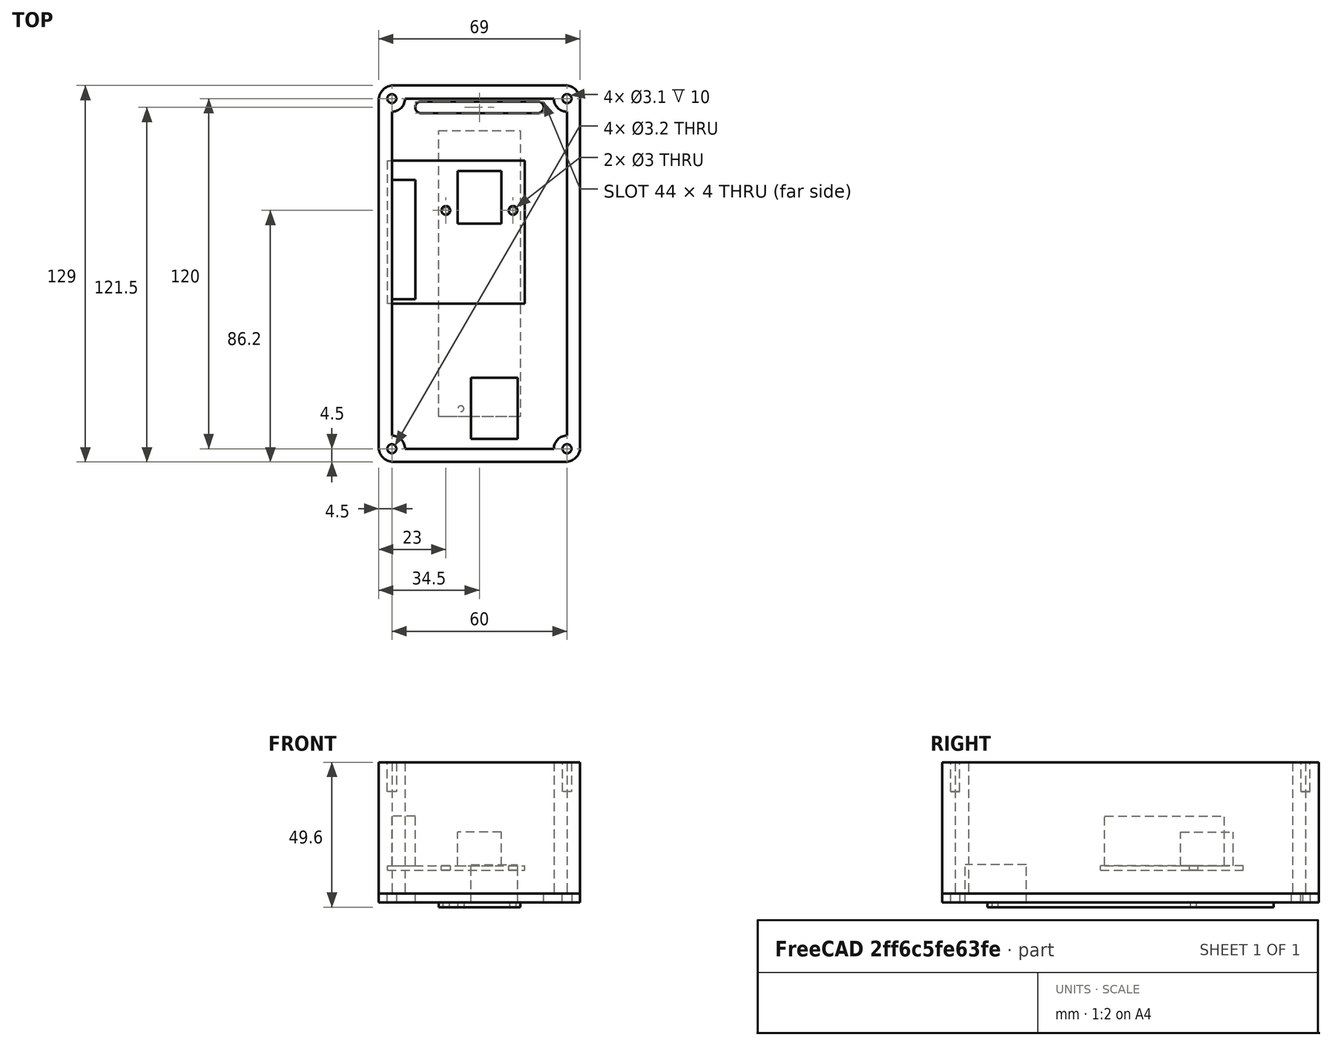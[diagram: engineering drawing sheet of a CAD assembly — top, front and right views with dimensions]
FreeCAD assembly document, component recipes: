
FREECAD ASSEMBLY — COMPONENT RECIPES ("Olimex_ESP32_POE_ISO_iot_case")

This assembly document has 3 components, labeled P0..P2 below (a component is one placed body or linked part). 3 of them carry a construction recipe — the FreeCAD feature program that regenerates the part from scratch, quoted from this document or its linked companion documents; the rest are supplied as boundary geometry only. No exploded tour is included for this assembly.
COMPONENT P0 — recipe-attached ("Box", modeled in this document).
Construction recipe (the document's own serialized feature program — sketch geometry with constraints, then the solid features built on it; lengths are millimeters unless a unit is written):

FEATURE [PartDesign::CoordinateSystem] LCS_0002
  AttacherType = Attacher::AttachEngine3D
  MapMode = 2
  Support = -> [X_Axis003]
FEATURE [PartDesign::Plane] DatumPlane002  label="Box Body Outer Bottom"
  Length = 87.869
  MapMode = 5
  ResizeMode = 0
  Support = -> [XY_Plane003]
  Width = 147.869
FEATURE [PartDesign::Plane] DatumPlane003  label="Box Body Inner Bottom"
  AttachmentOffset = pos=(0,0,3) rot=(0,0,1;0rad)
  Length = 87.869
  MapMode = 5
  Placement = pos=(0,0,3) rot=(0,0,1;0rad)
  ResizeMode = 0
  Support = -> [XY_Plane003]
  Width = 147.869
  expr: .AttachmentOffset.Base.z = Variables.base_thickness
FEATURE [PartDesign::Plane] DatumPlane004  label="Box Body Top"
  AttachmentOffset = pos=(0,0,45) rot=(0,0,1;0rad)
  Length = 87.869
  MapMode = 5
  Placement = pos=(0,0,48) rot=(0,0,1;0rad)
  ResizeMode = 0
  Support = -> [DatumPlane003]
  Width = 147.869
  expr: .AttachmentOffset.Base.z = Variables.inner_depth
FEATURE [Sketcher::SketchObject] Sketch002
  FullyConstrained = true
  MapMode = 5
  Support = -> [DatumPlane002]
  expr: .Constraints.height = Variables.inner_height + 2 * Variables.wall_thickness
  expr: .Constraints.width = Variables.inner_width + 2 * Variables.wall_thickness
  expr: Constraints[29] = Variables.corner_radius
  sketch-geometry (12):
    g0: LineSegment StartX=-34.5 StartY=64.5 StartZ=0 EndX=34.5 EndY=64.5 EndZ=0
    g1: LineSegment StartX=34.5 StartY=64.5 StartZ=0 EndX=34.5 EndY=-64.5 EndZ=0
    g2: LineSegment StartX=34.5 StartY=-64.5 StartZ=0 EndX=-34.5 EndY=-64.5 EndZ=0
    g3: LineSegment StartX=-34.5 StartY=-64.5 StartZ=0 EndX=-34.5 EndY=64.5 EndZ=0
    g4: LineSegment StartX=-29.5 StartY=64.5 StartZ=0 EndX=29.5 EndY=64.5 EndZ=0
    g5: LineSegment StartX=34.5 StartY=59.5 StartZ=0 EndX=34.5 EndY=-59.5 EndZ=0
    g6: LineSegment StartX=29.5 StartY=-64.5 StartZ=0 EndX=-29.5 EndY=-64.5 EndZ=0
    g7: LineSegment StartX=-34.5 StartY=-59.5 StartZ=0 EndX=-34.5 EndY=59.5 EndZ=0
    g8: ArcOfCircle CenterX=-29.5 CenterY=59.5 CenterZ=0 NormalX=0 NormalY=0 NormalZ=1 AngleXU=0 Radius=5 StartAngle=1.5708 EndAngle=3.14159
    g9: ArcOfCircle CenterX=-29.5 CenterY=-59.5 CenterZ=0 NormalX=0 NormalY=0 NormalZ=1 AngleXU=0 Radius=5 StartAngle=3.14159 EndAngle=4.71239
    g10: ArcOfCircle CenterX=29.5 CenterY=-59.5 CenterZ=0 NormalX=0 NormalY=0 NormalZ=1 AngleXU=0 Radius=5 StartAngle=4.71239 EndAngle=6.28319
    g11: ArcOfCircle CenterX=29.5 CenterY=59.5 CenterZ=0 NormalX=0 NormalY=0 NormalZ=1 AngleXU=0 Radius=5 StartAngle=0 EndAngle=1.5708
  constraints (30):
    c: Coincident(g0,g1)
    c: Coincident(g1,g2)
    c: Coincident(g2,g3)
    c: Coincident(g3,g0)
    c: Horizontal(g2)
    c: Vertical(g3)
    c: Symmetric(g0,g0,g-2)
    c: Symmetric(g0,g1,g-1)
    c: DistanceX(g0,g0) = 69  'width'
    c: DistanceY(g1,g1) = 129  'height'
    c: Horizontal(g4)
    c: Horizontal(g6)
    c: Vertical(g5)
    c: Vertical(g7)
    c: Tangent(g4,g8) = 1.5708
    c: Tangent(g7,g8) = 1.5708
    c: Tangent(g7,g9) = 1.5708
    c: Tangent(g6,g9) = 1.5708
    c: Tangent(g6,g10) = 1.5708
    c: Tangent(g5,g10) = 1.5708
    c: Tangent(g4,g11) = 1.5708
    c: Tangent(g5,g11) = 1.5708
    c: Equal(g8,g9)
    c: Equal(g9,g10)
    c: Equal(g10,g11)
    c: PointOnObject(g4,g0)
    c: PointOnObject(g7,g3)
    c: PointOnObject(g5,g1)
    c: PointOnObject(g6,g2)
    c: Radius(g9) = 5
FEATURE [PartDesign::Pad] Pad001  label="Box Body Volume"
  Direction = (0,0,1)
  Length = 10
  Length2 = 10
  Profile = -> Sketch002
  ReferenceAxis = -> Sketch002 [N_Axis]
  Type = 3
  UpToFace = -> DatumPlane004 [Plane]
FEATURE [Sketcher::SketchObject] Sketch003
  FullyConstrained = true
  MapMode = 5
  Placement = pos=(0,0,48) rot=(0,0,1;0rad)
  Support = -> [DatumPlane004]
  expr: .Constraints.height = Variables.inner_height
  expr: .Constraints.width = Variables.inner_width
  sketch-geometry (8):
    g0: LineSegment StartX=-30 StartY=60 StartZ=0 EndX=30 EndY=60 EndZ=0
    g1: LineSegment StartX=30 StartY=60 StartZ=0 EndX=30 EndY=-60 EndZ=0
    g2: LineSegment StartX=30 StartY=-60 StartZ=0 EndX=-30 EndY=-60 EndZ=0
    g3: LineSegment StartX=-30 StartY=-60 StartZ=0 EndX=-30 EndY=60 EndZ=0
    g4: LineSegment StartX=-30 StartY=60 StartZ=0 EndX=30 EndY=60 EndZ=0
    g5: LineSegment StartX=30 StartY=60 StartZ=0 EndX=30 EndY=-60 EndZ=0
    g6: LineSegment StartX=30 StartY=-60 StartZ=0 EndX=-30 EndY=-60 EndZ=0
    g7: LineSegment StartX=-30 StartY=-60 StartZ=0 EndX=-30 EndY=60 EndZ=0
  constraints (20):
    c: Coincident(g0,g1)
    c: Coincident(g1,g2)
    c: Coincident(g2,g3)
    c: Coincident(g3,g0)
    c: Horizontal(g2)
    c: Vertical(g3)
    c: Symmetric(g0,g0,g-2)
    c: Symmetric(g0,g1,g-1)
    c: DistanceX(g0,g0) = 60  'width'
    c: DistanceY(g1,g1) = 120  'height'
    c: Coincident(g4,g5)
    c: Coincident(g5,g6)
    c: Coincident(g6,g7)
    c: Coincident(g7,g4)
    c: Horizontal(g4)
    c: Horizontal(g6)
    c: Vertical(g5)
    c: Vertical(g7)
    c: Coincident(g4,g0)
    c: Coincident(g5,g1)
FEATURE [PartDesign::Pocket] Pocket001  label="Box Inner Volume"
  BaseFeature = -> Pad001
  Direction = (0,0,-1)
  Length = 0
  Length2 = 5
  Profile = -> Sketch003
  ReferenceAxis = -> Sketch003 [N_Axis]
  Type = 3
  UpToFace = -> DatumPlane003
FEATURE [Sketcher::SketchObject] Sketch004
  FullyConstrained = true
  MapMode = 5
  Placement = pos=(0,0,48) rot=(0,0,1;0rad)
  Support = -> [DatumPlane004]
  expr: .Constraints.height = Variables.inner_height
  expr: .Constraints.width = Variables.inner_width
  expr: Constraints[41] = Variables.wall_thickness
  sketch-geometry (16):
    g0: LineSegment StartX=-30 StartY=60 StartZ=0 EndX=30 EndY=60 EndZ=0
    g1: LineSegment StartX=30 StartY=60 StartZ=0 EndX=30 EndY=-60 EndZ=0
    g2: LineSegment StartX=30 StartY=-60 StartZ=0 EndX=-30 EndY=-60 EndZ=0
    g3: LineSegment StartX=-30 StartY=-60 StartZ=0 EndX=-30 EndY=60 EndZ=0
    g4: ArcOfCircle CenterX=-30 CenterY=60 CenterZ=0 NormalX=0 NormalY=0 NormalZ=1 AngleXU=0 Radius=4.5 StartAngle=4.71239 EndAngle=6.28319
    g5: LineSegment StartX=-30 StartY=60 StartZ=0 EndX=-30 EndY=55.5 EndZ=0
    g6: LineSegment StartX=-30 StartY=60 StartZ=0 EndX=-25.5 EndY=60 EndZ=0
    g7: ArcOfCircle CenterX=30 CenterY=60 CenterZ=0 NormalX=0 NormalY=0 NormalZ=1 AngleXU=0 Radius=4.5 StartAngle=3.14159 EndAngle=4.71239
    g8: ArcOfCircle CenterX=30 CenterY=-60 CenterZ=0 NormalX=0 NormalY=0 NormalZ=1 AngleXU=0 Radius=4.5 StartAngle=1.5708 EndAngle=3.14159
    g9: ArcOfCircle CenterX=-30 CenterY=-60 CenterZ=0 NormalX=0 NormalY=0 NormalZ=1 AngleXU=0 Radius=4.5 StartAngle=7e-16 EndAngle=1.5708
    g10: LineSegment StartX=-30 StartY=-55.5 StartZ=0 EndX=-30 EndY=-60 EndZ=0
    g11: LineSegment StartX=-30 StartY=-60 StartZ=0 EndX=-25.5 EndY=-60 EndZ=0
    g12: LineSegment StartX=30 StartY=-55.5 StartZ=0 EndX=30 EndY=-60 EndZ=0
    g13: LineSegment StartX=30 StartY=-60 StartZ=0 EndX=25.5 EndY=-60 EndZ=0
    g14: LineSegment StartX=25.5 StartY=60 StartZ=0 EndX=30 EndY=60 EndZ=0
    g15: LineSegment StartX=30 StartY=60 StartZ=0 EndX=30 EndY=55.5 EndZ=0
  constraints (42):
    c: Coincident(g0,g1)
    c: Coincident(g1,g2)
    c: Coincident(g2,g3)
    c: Coincident(g3,g0)
    c: Horizontal(g2)
    c: Vertical(g3)
    c: Symmetric(g0,g0,g-2)
    c: Symmetric(g0,g1,g-1)
    c: DistanceX(g0,g0) = 60  'width'
    c: DistanceY(g1,g1) = 120  'height'
    c: Coincident(g4,g0)
    c: PointOnObject(g4,g0)
    c: PointOnObject(g4,g3)
    c: Coincident(g5,g4)
    c: Coincident(g5,g4)
    c: Coincident(g6,g4)
    c: Coincident(g6,g4)
    c: Coincident(g7,g0)
    c: PointOnObject(g7,g1)
    c: PointOnObject(g7,g0)
    c: Coincident(g8,g1)
    c: PointOnObject(g8,g1)
    c: PointOnObject(g8,g2)
    c: Coincident(g9,g2)
    c: PointOnObject(g9,g3)
    c: PointOnObject(g9,g2)
    c: Coincident(g10,g9)
    c: Coincident(g10,g9)
    c: Coincident(g11,g9)
    c: Coincident(g11,g9)
    c: Coincident(g12,g8)
    c: Coincident(g12,g8)
    c: Coincident(g13,g8)
    c: Coincident(g13,g8)
    c: Coincident(g14,g7)
    c: Coincident(g14,g7)
    c: Coincident(g15,g7)
    c: Coincident(g15,g7)
    c: Equal(g4,g7)
    c: Equal(g7,g8)
    c: Equal(g8,g9)
    c: Radius(g9) = 4.5
FEATURE [PartDesign::Pad] Pad002  label="Box Inner Mounting Hole Supports"
  BaseFeature = -> Pocket001
  Direction = (0,0,1)
  Length = 10
  Length2 = 10
  Profile = -> Sketch004
  ReferenceAxis = -> Sketch004 [N_Axis]
  Type = 3
  UpToFace = -> DatumPlane003
FEATURE [Sketcher::SketchObject] Sketch005
  FullyConstrained = true
  MapMode = 5
  Placement = pos=(0,0,48) rot=(0,0,1;0rad)
  Support = -> [DatumPlane004]
  expr: .Constraints.height = Variables.inner_height
  expr: .Constraints.width = Variables.inner_width
  expr: Constraints[17] = Variables.box_mounting_hole_diameter
  sketch-geometry (8):
    g0: LineSegment StartX=-30 StartY=60 StartZ=0 EndX=30 EndY=60 EndZ=0
    g1: LineSegment StartX=30 StartY=60 StartZ=0 EndX=30 EndY=-60 EndZ=0
    g2: LineSegment StartX=30 StartY=-60 StartZ=0 EndX=-30 EndY=-60 EndZ=0
    g3: LineSegment StartX=-30 StartY=-60 StartZ=0 EndX=-30 EndY=60 EndZ=0
    g4: Circle CenterX=-30 CenterY=60 CenterZ=0 NormalX=0 NormalY=0 NormalZ=1 AngleXU=0 Radius=1.55
    g5: Circle CenterX=30 CenterY=60 CenterZ=0 NormalX=0 NormalY=0 NormalZ=1 AngleXU=0 Radius=1.55
    g6: Circle CenterX=30 CenterY=-60 CenterZ=0 NormalX=0 NormalY=0 NormalZ=1 AngleXU=0 Radius=1.55
    g7: Circle CenterX=-30 CenterY=-60 CenterZ=0 NormalX=0 NormalY=0 NormalZ=1 AngleXU=0 Radius=1.55
  constraints (18):
    c: Coincident(g0,g1)
    c: Coincident(g1,g2)
    c: Coincident(g2,g3)
    c: Coincident(g3,g0)
    c: Horizontal(g2)
    c: Vertical(g3)
    c: Coincident(g4,g0)
    c: Coincident(g5,g0)
    c: Coincident(g6,g1)
    c: Coincident(g7,g2)
    c: Symmetric(g4,g5,g-2)
    c: Symmetric(g5,g6,g-1)
    c: DistanceX(g0,g0) = 60  'width'
    c: DistanceY(g1,g1) = 120  'height'
    c: Equal(g4,g5)
    c: Equal(g5,g6)
    c: Equal(g6,g7)
    c: Diameter(g7) = 3.1
FEATURE [PartDesign::Plane] DatumPlane005  label="Box Mounting Hole Depth"
  AttachmentOffset = pos=(0,0,-10) rot=(0,0,1;0rad)
  Length = 87.869
  MapMode = 5
  Placement = pos=(0,0,38) rot=(0,0,1;0rad)
  ResizeMode = 0
  Support = -> [DatumPlane004]
  Width = 147.869
  expr: .AttachmentOffset.Base.z = -Variables.box_mounting_hole_depth
FEATURE [PartDesign::Pocket] Pocket002  label="Box Mounting Holes"
  BaseFeature = -> Pad002
  Direction = (0,0,-1)
  Length = 0
  Length2 = 5
  Profile = -> Sketch005
  ReferenceAxis = -> Sketch005 [N_Axis]
  Type = 3
  UpToFace = -> DatumPlane005 [Plane]
FEATURE [PartDesign::CoordinateSystem] Local_CS001  label="Box Body Lower Left Mounting Hole Top"
  AttacherType = Attacher::AttachEngine3D
  MapMode = 45
  Placement = pos=(-30,-60,48) rot=(0,0,1;0rad)
  Support = -> [Pocket002]
FEATURE [PartDesign::Plane] DatumPlane006  label="Box Body Front Inner"
  AttachmentOffset = pos=(0,0,60) rot=(0,0,1;0rad)
  Length = 83.1944
  MapMode = 5
  Placement = pos=(0,-60,-1.33e-14) rot=(1,0,0;1.5708rad)
  ResizeMode = 0
  Support = -> [XZ_Plane003]
  Width = 87.1944
  expr: .AttachmentOffset.Base.z = Variables.inner_height / 2
FEATURE [PartDesign::Plane] DatumPlane007  label="Box Body Rear Inner"
  AttachmentOffset = pos=(0,0,-60) rot=(0,0,1;0rad)
  Length = 83.1944
  MapMode = 5
  Placement = pos=(0,60,1.33e-14) rot=(1,0,0;1.5708rad)
  ResizeMode = 0
  Support = -> [XZ_Plane003]
  Width = 87.1944
  expr: .AttachmentOffset.Base.z = -Variables.inner_height / 2
FEATURE [PartDesign::Plane] DatumPlane008  label="Box Body Front Outer"
  AttachmentOffset = pos=(0,0,4.5) rot=(0,0,1;0rad)
  Length = 83.1944
  MapMode = 5
  Placement = pos=(0,-64.5,-1.43e-14) rot=(1,0,0;1.5708rad)
  ResizeMode = 0
  Support = -> [DatumPlane006]
  Width = 87.1944
  expr: .AttachmentOffset.Base.z = Variables.wall_thickness
FEATURE [PartDesign::Plane] DatumPlane009  label="Box Body Rear Outer"
  AttachmentOffset = pos=(0,0,-4.5) rot=(0,0,1;0rad)
  Length = 83.1944
  MapMode = 5
  Placement = pos=(0,64.5,1.43e-14) rot=(1,0,0;1.5708rad)
  ResizeMode = 0
  Support = -> [DatumPlane007]
  Width = 87.1944
  expr: .AttachmentOffset.Base.z = -Variables.wall_thickness
FEATURE [PartDesign::Plane] DatumPlane010  label="Box Body Right Inner"
  AttachmentOffset = pos=(0,0,30) rot=(0,0,1;0rad)
  Length = 148.408
  MapMode = 5
  Placement = pos=(30,-6.7e-15,6.7e-15) rot=(0.57735,0.57735,0.57735;2.0944rad)
  ResizeMode = 0
  Support = -> [YZ_Plane003]
  Width = 92.4082
  expr: .AttachmentOffset.Base.z = Variables.inner_width / 2
FEATURE [PartDesign::Plane] DatumPlane011  label="Box Body Right Outer"
  AttachmentOffset = pos=(0,0,4.5) rot=(0,0,1;0rad)
  Length = 148.408
  MapMode = 5
  Placement = pos=(34.5,-7.2e-15,7.2e-15) rot=(0.57735,0.57735,0.57735;2.0944rad)
  ResizeMode = 0
  Support = -> [DatumPlane010]
  Width = 92.4082
  expr: .AttachmentOffset.Base.z = Variables.wall_thickness
FEATURE [PartDesign::Plane] DatumPlane012  label="Box Body Left Inner"
  AttachmentOffset = pos=(0,0,-30) rot=(0,0,1;0rad)
  Length = 148.408
  MapMode = 5
  Placement = pos=(-30,6.7e-15,-6.7e-15) rot=(0.57735,0.57735,0.57735;2.0944rad)
  ResizeMode = 0
  Support = -> [YZ_Plane003]
  Width = 92.4082
  expr: .AttachmentOffset.Base.z = -Variables.inner_width / 2
FEATURE [PartDesign::Plane] DatumPlane013  label="Box Body Left Outer"
  AttachmentOffset = pos=(0,0,-4.5) rot=(0,0,1;0rad)
  Length = 148.408
  MapMode = 5
  Placement = pos=(-34.5,7.2e-15,-7.2e-15) rot=(0.57735,0.57735,0.57735;2.0944rad)
  ResizeMode = 0
  Support = -> [DatumPlane012]
  Width = 92.4082
  expr: .AttachmentOffset.Base.z = -Variables.wall_thickness
FEATURE [PartDesign::Point] DatumPoint  label="Box Body Olimex Board Lower Mounting Hole Position"
  AttacherType = Attacher::AttachEnginePoint
  AttachmentOffset = pos=(3,-55,0) rot=(0,0,1;0rad)
  MapMode = 32
  Placement = pos=(3,-55,3) rot=(0,0,1;0rad)
  Support = -> [DatumPlane003]
FEATURE [PartDesign::AdditiveCone] Cone  label="Box Body Olimex Board Lower Mounting Hole Standoff"
  Angle = 360
  AttacherType = Attacher::AttachEngine3D
  BaseFeature = -> Pocket002
  Height = 6
  MapMode = 1
  Placement = pos=(3,-55,3) rot=(0,0,1;0rad)
  Radius1 = 4
  Radius2 = 2
  Support = -> [DatumPoint]
FEATURE [PartDesign::Point] DatumPoint001  label="Box Body Olimex Board Upper Left Mounting Hole Position"
  AttacherType = Attacher::AttachEnginePoint
  AttachmentOffset = pos=(-5.07,67.94,0) rot=(0,0,1;0rad)
  MapMode = 39
  Placement = pos=(-2.07,12.94,3) rot=(0,0,1;0rad)
  Support = -> [DatumPoint]
  expr: .AttachmentOffset.Base.x = <<Sketch007>>.Constraints.x_upper_left - <<Sketch007>>.Constraints.x_lower
  expr: .AttachmentOffset.Base.y = <<Sketch007>>.Constraints.y_upper - <<Sketch007>>.Constraints.y_lower
FEATURE [PartDesign::AdditiveCone] Cone001  label="Box Body Olimex Board Upper Left Mounting Hole Standoff"
  Angle = 360
  AttacherType = Attacher::AttachEngine3D
  BaseFeature = -> Cone
  Height = 6
  MapMode = 1
  Placement = pos=(-2.07,12.94,3) rot=(0,0,1;0rad)
  Radius1 = 4
  Radius2 = 2
  Support = -> [DatumPoint001]
  expr: Height = <<Box Body Olimex Board Lower Mounting Hole Standoff>>.Height
  expr: Radius1 = <<Box Body Olimex Board Lower Mounting Hole Standoff>>.Radius1
  expr: Radius2 = <<Box Body Olimex Board Lower Mounting Hole Standoff>>.Radius2
FEATURE [PartDesign::Point] DatumPoint002  label="Box Body Olimex Board Upper Right Mounting Hole Position"
  AttacherType = Attacher::AttachEnginePoint
  AttachmentOffset = pos=(17.79,67.94,0) rot=(0,0,1;0rad)
  MapMode = 39
  Placement = pos=(20.79,12.94,3) rot=(0,0,1;0rad)
  Support = -> [DatumPoint]
  expr: .AttachmentOffset.Base.x = <<Sketch007>>.Constraints.x_upper_right - <<Sketch007>>.Constraints.x_lower
  expr: .AttachmentOffset.Base.y = <<Sketch007>>.Constraints.y_upper - <<Sketch007>>.Constraints.y_lower
FEATURE [PartDesign::AdditiveCone] Cone002  label="Box Body Olimex Board Upper Right Mounting Hole Standoff"
  Angle = 360
  AttacherType = Attacher::AttachEngine3D
  BaseFeature = -> Cone001
  Height = 6
  MapMode = 1
  Placement = pos=(20.79,12.94,3) rot=(0,0,1;0rad)
  Radius1 = 4
  Radius2 = 2
  Support = -> [DatumPoint002]
  expr: Height = <<Box Body Olimex Board Lower Mounting Hole Standoff>>.Height
  expr: Radius1 = <<Box Body Olimex Board Lower Mounting Hole Standoff>>.Radius1
  expr: Radius2 = <<Box Body Olimex Board Lower Mounting Hole Standoff>>.Radius2
FEATURE [PartDesign::Plane] DatumPlane014  label="Box Body Olimes Board Standoff Height"
  AttachmentOffset = pos=(0,0,6) rot=(0,0,1;0rad)
  Length = 87.869
  MapMode = 5
  Placement = pos=(0,0,9) rot=(0,0,1;0rad)
  ResizeMode = 0
  Support = -> [DatumPlane003]
  Width = 147.869
  expr: .AttachmentOffset.Base.z = <<Box Body Olimex Board Lower Mounting Hole Standoff>>.Height
FEATURE [PartDesign::Point] DatumPoint003  label="Box Body Olimex Board Lower Mounting Hole Position Top"
  AttacherType = Attacher::AttachEnginePoint
  MapMode = 40
  Placement = pos=(3,-55,9) rot=(0,0,1;0rad)
  Support = -> [DatumPlane014,DatumPoint]
FEATURE [PartDesign::Point] DatumPoint004  label="Box Body Olimex Board Upper Left Mounting Hole Position Top"
  AttacherType = Attacher::AttachEnginePoint
  MapMode = 40
  Placement = pos=(-2.07,12.94,9) rot=(0,0,1;0rad)
  Support = -> [DatumPlane014,DatumPoint001]
FEATURE [PartDesign::Plane] DatumPlane015  label="Box Body Olimex Board Mounting Holes Depth"
  AttachmentOffset = pos=(0,0,-1) rot=(0,0,1;0rad)
  Length = 87.869
  MapMode = 5
  Placement = pos=(0,0,2) rot=(0,0,1;0rad)
  ResizeMode = 0
  Support = -> [DatumPlane003]
  Width = 147.869
FEATURE [Sketcher::SketchObject] Sketch010
  FullyConstrained = true
  MapMode = 5
  Placement = pos=(0,-64.5,-1.43e-14) rot=(1,0,0;1.5708rad)
  Support = -> [DatumPlane008]
  expr: Constraints[8] = <<Sketch008>>.Constraints.rj45_width + 2mm
  expr: Constraints[9] = <<Olimex ESP32-POE-ISO RJ45>>.Length + 2mm
  sketch-geometry (8):
    g0: LineSegment StartX=5.5 StartY=24.5 StartZ=0 EndX=23.5 EndY=24.5 EndZ=0
    g1: LineSegment StartX=23.5 StartY=24.5 StartZ=0 EndX=23.5 EndY=9.5 EndZ=0
    g2: LineSegment StartX=23.5 StartY=9.5 StartZ=0 EndX=5.5 EndY=9.5 EndZ=0
    g3: LineSegment StartX=5.5 StartY=9.5 StartZ=0 EndX=5.5 EndY=24.5 EndZ=0
    g4: ArcOfCircle CenterX=-15 CenterY=21 CenterZ=0 NormalX=0 NormalY=0 NormalZ=1 AngleXU=0 Radius=9 StartAngle=5.1e-15 EndAngle=3.14159
    g5: ArcOfCircle CenterX=-15 CenterY=15 CenterZ=0 NormalX=0 NormalY=0 NormalZ=1 AngleXU=0 Radius=9 StartAngle=3.14159 EndAngle=6.28319
    g6: LineSegment StartX=-24 StartY=21 StartZ=0 EndX=-24 EndY=15 EndZ=0
    g7: LineSegment StartX=-6 StartY=15 StartZ=0 EndX=-6 EndY=21 EndZ=0
  constraints (22):
    c: Coincident(g0,g1)
    c: Coincident(g1,g2)
    c: Coincident(g2,g3)
    c: Coincident(g3,g0)
    c: Horizontal(g0)
    c: Horizontal(g2)
    c: Vertical(g1)
    c: Vertical(g3)
    c: DistanceX(g0,g0) = 18
    c: DistanceY(g1,g1) = 15
    c: DistanceX(g-1,g2) = 5.5
    c: DistanceY(g-1,g2) = 9.5
    c: Tangent(g4,g6) = -1.5708
    c: Tangent(g6,g5) = -1.5708
    c: Tangent(g5,g7) = -1.5708
    c: Tangent(g7,g4) = -1.5708
    c: Equal(g4,g5)
    c: Vertical(g6)
    c: DistanceX(g5,g-1) = 15
    c: Radius(g4) = 9
    c: DistanceY(g-1,g5) = 15
    c: DistanceY(g5,g4) = 6
FEATURE [PartDesign::Body] Box_Body  label="Box Body"
  Group = -> [LCS_0002,DatumPlane002,DatumPlane003,DatumPlane004,Sketch002,Pad001,Sketch003,Pocket001,Sketch004,Pad002,Sketch005,DatumPlane005,Pocket002,Local_CS001,DatumPlane006,DatumPlane008,DatumPlane007,DatumPlane009,DatumPlane010,DatumPlane011,DatumPlane012,DatumPlane013,DatumPoint,DatumPoint001,DatumPoint002,DatumPlane015,Sketch010,Cone,Cone001,Cone002,DatumPlane014,DatumPoint003,DatumPoint004,+7 more]
  Origin = -> Origin003
  Tip = -> Pocket002
COMPONENT P1 — recipe-attached ("Lid", modeled in this document).
Construction recipe (the document's own serialized feature program — sketch geometry with constraints, then the solid features built on it; lengths are millimeters unless a unit is written):

FEATURE [PartDesign::Plane] DatumPlane  label="Lid Panel Bottom"
  Length = 87.869
  MapMode = 5
  ResizeMode = 0
  Support = -> [XY_Plane004]
  Width = 147.869
FEATURE [PartDesign::Plane] DatumPlane001  label="Lid Panel Top"
  AttachmentOffset = pos=(0,0,3) rot=(0,0,1;0rad)
  Length = 87.869
  MapMode = 5
  Placement = pos=(0,0,3) rot=(0,0,1;0rad)
  ResizeMode = 0
  Support = -> [XY_Plane004]
  Width = 147.869
  expr: .AttachmentOffset.Base.z = Variables.lid_thickness
FEATURE [Sketcher::SketchObject] Sketch
  FullyConstrained = true
  MapMode = 5
  Support = -> [DatumPlane]
  expr: .Constraints.height = Variables.inner_height + 2 * Variables.wall_thickness
  expr: .Constraints.width = <<Variables>>.inner_width + 2 * Variables.wall_thickness
  expr: Constraints[29] = Variables.corner_radius
  sketch-geometry (12):
    g0: LineSegment StartX=-34.5 StartY=64.5 StartZ=0 EndX=34.5 EndY=64.5 EndZ=0
    g1: LineSegment StartX=34.5 StartY=64.5 StartZ=0 EndX=34.5 EndY=-64.5 EndZ=0
    g2: LineSegment StartX=34.5 StartY=-64.5 StartZ=0 EndX=-34.5 EndY=-64.5 EndZ=0
    g3: LineSegment StartX=-34.5 StartY=-64.5 StartZ=0 EndX=-34.5 EndY=64.5 EndZ=0
    g4: LineSegment StartX=-29.5 StartY=64.5 StartZ=0 EndX=29.5 EndY=64.5 EndZ=0
    g5: LineSegment StartX=34.5 StartY=59.5 StartZ=0 EndX=34.5 EndY=-59.5 EndZ=0
    g6: LineSegment StartX=29.5 StartY=-64.5 StartZ=0 EndX=-29.5 EndY=-64.5 EndZ=0
    g7: LineSegment StartX=-34.5 StartY=-59.5 StartZ=0 EndX=-34.5 EndY=59.5 EndZ=0
    g8: ArcOfCircle CenterX=-29.5 CenterY=59.5 CenterZ=0 NormalX=0 NormalY=0 NormalZ=1 AngleXU=0 Radius=5 StartAngle=1.5708 EndAngle=3.14159
    g9: ArcOfCircle CenterX=-29.5 CenterY=-59.5 CenterZ=0 NormalX=0 NormalY=0 NormalZ=1 AngleXU=0 Radius=5 StartAngle=3.14159 EndAngle=4.71239
    g10: ArcOfCircle CenterX=29.5 CenterY=-59.5 CenterZ=0 NormalX=0 NormalY=0 NormalZ=1 AngleXU=0 Radius=5 StartAngle=4.71239 EndAngle=6.28319
    g11: ArcOfCircle CenterX=29.5 CenterY=59.5 CenterZ=0 NormalX=0 NormalY=0 NormalZ=1 AngleXU=0 Radius=5 StartAngle=5e-16 EndAngle=1.5708
  constraints (30):
    c: Coincident(g0,g1)
    c: Coincident(g1,g2)
    c: Coincident(g2,g3)
    c: Coincident(g3,g0)
    c: Horizontal(g2)
    c: Vertical(g3)
    c: Symmetric(g0,g0,g-2)
    c: Symmetric(g0,g1,g-1)
    c: DistanceX(g0,g0) = 69  'width'
    c: DistanceY(g1,g1) = 129  'height'
    c: Horizontal(g4)
    c: Horizontal(g6)
    c: Vertical(g5)
    c: Vertical(g7)
    c: Tangent(g4,g8) = 1.5708
    c: Tangent(g7,g8) = 1.5708
    c: Tangent(g7,g9) = 1.5708
    c: Tangent(g6,g9) = 1.5708
    c: Tangent(g6,g10) = 1.5708
    c: Tangent(g5,g10) = 1.5708
    c: Tangent(g5,g11) = 1.5708
    c: Tangent(g4,g11) = 1.5708
    c: PointOnObject(g4,g0)
    c: PointOnObject(g7,g3)
    c: PointOnObject(g5,g1)
    c: PointOnObject(g6,g2)
    c: Equal(g8,g9)
    c: Equal(g9,g10)
    c: Equal(g10,g11)
    c: Radius(g9) = 5
FEATURE [PartDesign::Pad] Pad  label="Lid Panel"
  Direction = (0,0,1)
  Length = 10
  Length2 = 10
  Profile = -> Sketch
  ReferenceAxis = -> Sketch [N_Axis]
  Type = 3
  UpToFace = -> DatumPlane001 [Plane]
FEATURE [Sketcher::SketchObject] Sketch001
  FullyConstrained = true
  MapMode = 5
  Placement = pos=(0,0,3) rot=(0,0,1;0rad)
  Support = -> [DatumPlane001]
  expr: Constraints[17] = Variables.lid_mounting_hole_diameter
  expr: Constraints[8] = Variables.inner_width
  expr: Constraints[9] = Variables.inner_height
  sketch-geometry (8):
    g0: LineSegment StartX=-30 StartY=60 StartZ=0 EndX=30 EndY=60 EndZ=0
    g1: LineSegment StartX=30 StartY=60 StartZ=0 EndX=30 EndY=-60 EndZ=0
    g2: LineSegment StartX=30 StartY=-60 StartZ=0 EndX=-30 EndY=-60 EndZ=0
    g3: LineSegment StartX=-30 StartY=-60 StartZ=0 EndX=-30 EndY=60 EndZ=0
    g4: Circle CenterX=-30 CenterY=60 CenterZ=0 NormalX=0 NormalY=0 NormalZ=1 AngleXU=0 Radius=1.6
    g5: Circle CenterX=30 CenterY=60 CenterZ=0 NormalX=0 NormalY=0 NormalZ=1 AngleXU=0 Radius=1.6
    g6: Circle CenterX=30 CenterY=-60 CenterZ=0 NormalX=0 NormalY=0 NormalZ=1 AngleXU=0 Radius=1.6
    g7: Circle CenterX=-30 CenterY=-60 CenterZ=0 NormalX=0 NormalY=0 NormalZ=1 AngleXU=0 Radius=1.6
  constraints (18):
    c: Coincident(g0,g1)
    c: Coincident(g1,g2)
    c: Coincident(g2,g3)
    c: Coincident(g3,g0)
    c: Horizontal(g2)
    c: Vertical(g3)
    c: Symmetric(g0,g0,g-2)
    c: Symmetric(g0,g1,g-1)
    c: DistanceX(g0,g0) = 60
    c: DistanceY(g1,g1) = 120
    c: Coincident(g4,g0)
    c: Coincident(g5,g0)
    c: Coincident(g6,g1)
    c: Coincident(g7,g2)
    c: Equal(g4,g5)
    c: Equal(g5,g6)
    c: Equal(g6,g7)
    c: Diameter(g7) = 3.2
FEATURE [PartDesign::Pocket] Pocket  label="Lid Mounting Holes"
  BaseFeature = -> Pad
  Direction = (0,0,-1)
  Length = 0
  Length2 = 5
  Profile = -> Sketch001
  ReferenceAxis = -> Sketch001 [N_Axis]
  Type = 3
  UpToFace = -> DatumPlane [Plane]
FEATURE [PartDesign::CoordinateSystem] Local_CS  label="Lid Body Lower Left Mounting Hole Bottom"
  AttacherType = Attacher::AttachEngine3D
  MapMode = 45
  Placement = pos=(-30,-60,0) rot=(0,0,-1;8e-05rad)
  Support = -> [Pocket]
FEATURE [Sketcher::SketchObject] Sketch014
  FullyConstrained = true
  MapMode = 5
  Placement = pos=(0,0,3) rot=(0,0,1;0rad)
  Support = -> [DatumPlane001]
  sketch-geometry (4):
    g0: ArcOfCircle CenterX=-20 CenterY=57 CenterZ=0 NormalX=0 NormalY=0 NormalZ=1 AngleXU=0 Radius=2 StartAngle=1.5708 EndAngle=4.71239
    g1: ArcOfCircle CenterX=20 CenterY=57 CenterZ=0 NormalX=0 NormalY=0 NormalZ=1 AngleXU=0 Radius=2 StartAngle=4.71239 EndAngle=7.85398
    g2: LineSegment StartX=-20 StartY=55 StartZ=0 EndX=20 EndY=55 EndZ=0
    g3: LineSegment StartX=20 StartY=59 StartZ=0 EndX=-20 EndY=59 EndZ=0
  constraints (9):
    c: Tangent(g0,g2) = -1.5708
    c: Tangent(g2,g1) = -1.5708
    c: Tangent(g1,g3) = -1.5708
    c: Tangent(g3,g0) = -1.5708
    c: Equal(g0,g1)
    c: Symmetric(g0,g1,g-2)
    c: Radius(g1) = 2
    c: DistanceX(g0,g1) = 40
    c: DistanceY(g-1,g0) = 57
FEATURE [PartDesign::Pocket] Pocket008  label="Lid Body Cooling Slot"
  BaseFeature = -> Pocket
  Direction = (0,0,-1)
  Length = 0
  Length2 = 5
  Profile = -> Sketch014
  ReferenceAxis = -> Sketch014 [N_Axis]
  Type = 3
  UpToFace = -> DatumPlane [Plane]
FEATURE [PartDesign::Body] Lid_Body  label="Lid Body"
  Group = -> [DatumPlane,DatumPlane001,Sketch,Pad,Sketch001,Pocket,Local_CS,Sketch014,Pocket008]
  Origin = -> Origin004
  Tip = -> Pocket008
COMPONENT P2 — recipe-attached ("Olimex ESP32-POE-ISO", modeled in this document).
Construction recipe (the document's own serialized feature program — sketch geometry with constraints, then the solid features built on it; lengths are millimeters unless a unit is written):

FEATURE [Sketcher::SketchObject] Sketch006
  FullyConstrained = true
  MapMode = 5
  Support = -> [XY_Plane006]
  sketch-geometry (4):
    g0: LineSegment StartX=-14 StartY=49 StartZ=0 EndX=14 EndY=49 EndZ=0
    g1: LineSegment StartX=14 StartY=49 StartZ=0 EndX=14 EndY=-49 EndZ=0
    g2: LineSegment StartX=14 StartY=-49 StartZ=0 EndX=-14 EndY=-49 EndZ=0
    g3: LineSegment StartX=-14 StartY=-49 StartZ=0 EndX=-14 EndY=49 EndZ=0
  constraints (10):
    c: Coincident(g0,g1)
    c: Coincident(g1,g2)
    c: Coincident(g2,g3)
    c: Coincident(g3,g0)
    c: Horizontal(g2)
    c: Vertical(g3)
    c: Symmetric(g0,g0,g-2)
    c: Symmetric(g0,g1,g-1)
    c: DistanceX(g0,g0) = 28
    c: DistanceY(g3,g3) = 98
FEATURE [PartDesign::Pad] Pad003  label="Olimex ESP32-POE-ISO PCB"
  Direction = (0,0,1)
  Length = 1.6
  Length2 = 10
  Profile = -> Sketch006
  ReferenceAxis = -> Sketch006 [N_Axis]
  Reversed = true
  Type = 0
FEATURE [Sketcher::SketchObject] Sketch007
  ExternalGeometry = -> [Pad003]
  FullyConstrained = true
  MapMode = 5
  Support = -> [XY_Plane006]
  sketch-geometry (3):
    g0: Circle CenterX=-11.43 CenterY=21.67 CenterZ=0 NormalX=0 NormalY=0 NormalZ=1 AngleXU=0 Radius=1
    g1: Circle CenterX=11.43 CenterY=21.67 CenterZ=0 NormalX=0 NormalY=0 NormalZ=1 AngleXU=0 Radius=1
    g2: Circle CenterX=-6.36 CenterY=-46.27 CenterZ=0 NormalX=0 NormalY=0 NormalZ=1 AngleXU=0 Radius=1
  constraints (9):
    c: Equal(g0,g1)
    c: Equal(g1,g2)
    c: Diameter(g1) = 2
    c: Horizontal(g0,g1)
    c: DistanceY(g-6,g1) = 70.67  'y_upper'
    c: DistanceX(g-6,g2) = 7.64  'x_lower'
    c: DistanceY(g-6,g2) = 2.73  'y_lower'
    c: DistanceX(g-5,g1) = 25.43  'x_upper_right'
    c: DistanceX(g-5,g0) = 2.57  'x_upper_left'
FEATURE [PartDesign::Pocket] Pocket003  label="Olimex ESP32-POE-ISO Mounting Holes"
  BaseFeature = -> Pad003
  Direction = (0,0,-1)
  Length = 5
  Length2 = 5
  Profile = -> Sketch007
  ReferenceAxis = -> Sketch007 [N_Axis]
  Type = 1
FEATURE [Sketcher::SketchObject] Sketch008
  ExternalGeometry = -> [Pocket003]
  FullyConstrained = true
  MapMode = 5
  Support = -> [XY_Plane006]
  sketch-geometry (7):
    g0: LineSegment StartX=-2.95 StartY=-35.64 StartZ=0 EndX=13.05 EndY=-35.64 EndZ=0
    g1: LineSegment StartX=13.05 StartY=-35.64 StartZ=0 EndX=13.05 EndY=-56.64 EndZ=0
    g2: LineSegment StartX=13.05 StartY=-56.64 StartZ=0 EndX=-2.95 EndY=-56.64 EndZ=0
    g3: LineSegment StartX=-2.95 StartY=-56.64 StartZ=0 EndX=-2.95 EndY=-35.64 EndZ=0
    g4: LineSegment StartX=13.05 StartY=-35.64 StartZ=0 EndX=-2.95 EndY=-56.64 EndZ=0
    g5: LineSegment StartX=-2.95 StartY=-35.64 StartZ=0 EndX=13.05 EndY=-56.64 EndZ=0
    g6: GeomPoint X=5.05 Y=-46.14 Z=0
  constraints (18):
    c: Coincident(g0,g1)
    c: Coincident(g1,g2)
    c: Coincident(g2,g3)
    c: Coincident(g3,g0)
    c: Horizontal(g0)
    c: Horizontal(g2)
    c: Vertical(g1)
    c: Vertical(g3)
    c: Coincident(g4,g0)
    c: Coincident(g4,g2)
    c: Coincident(g5,g0)
    c: Coincident(g5,g1)
    c: PointOnObject(g6,g4)
    c: PointOnObject(g6,g5)
    c: DistanceX(g-4,g6) = 19.05
    c: DistanceY(g-5,g6) = 2.86
    c: DistanceY(g1,g1) = 21
    c: DistanceX(g2,g2) = 16  'rj45_width'
FEATURE [PartDesign::Pad] Pad004  label="Olimex ESP32-POE-ISO RJ45"
  BaseFeature = -> Pocket003
  Direction = (0,0,1)
  Length = 13
  Length2 = 10
  Profile = -> Sketch008
  ReferenceAxis = -> Sketch008 [N_Axis]
  Type = 0
FEATURE [PartDesign::CoordinateSystem] Local_CS002  label="Olimex ESP32-POE-ISO Lower Mounting Hole Bottom Body"
  AttacherType = Attacher::AttachEngine3D
  MapMode = 45
  Placement = pos=(-6.36,-46.27,-1.6) rot=(0,0,1;2.1e-05rad)
  Support = -> [Pad004]
FEATURE [PartDesign::Body] PCB  label="Olimex ESP32-POE-ISO Body"
  Group = -> [Sketch006,Pad003,Sketch007,Pocket003,Sketch008,Pad004,Local_CS002]
  Origin = -> Origin006
  Tip = -> Pad004
FEATURE [PartDesign::Plane] DatumPlane016  label="Olimex Breakout Board Bottom"
  Length = 60
  MapMode = 5
  ResizeMode = 0
  Support = -> [XY_Plane007]
  Width = 60
FEATURE [Sketcher::SketchObject] Sketch011
  FullyConstrained = true
  MapMode = 5
  Support = -> [DatumPlane016]
  sketch-geometry (4):
    g0: LineSegment StartX=-23.5 StartY=24.5 StartZ=0 EndX=23.5 EndY=24.5 EndZ=0
    g1: LineSegment StartX=23.5 StartY=24.5 StartZ=0 EndX=23.5 EndY=-24.5 EndZ=0
    g2: LineSegment StartX=23.5 StartY=-24.5 StartZ=0 EndX=-23.5 EndY=-24.5 EndZ=0
    g3: LineSegment StartX=-23.5 StartY=-24.5 StartZ=0 EndX=-23.5 EndY=24.5 EndZ=0
  constraints (10):
    c: Coincident(g0,g1)
    c: Coincident(g1,g2)
    c: Coincident(g2,g3)
    c: Coincident(g3,g0)
    c: Horizontal(g2)
    c: Vertical(g3)
    c: DistanceX(g0,g0) = 47
    c: DistanceY(g1,g1) = 49
    c: Symmetric(g0,g0,g-2)
    c: Symmetric(g0,g1,g-1)
FEATURE [PartDesign::Plane] DatumPlane017  label="Olimex Breakout Board Top"
  AttachmentOffset = pos=(0,0,1.6) rot=(0,0,1;0rad)
  Length = 60
  MapMode = 5
  Placement = pos=(0,0,1.6) rot=(0,0,1;0rad)
  ResizeMode = 0
  Support = -> [DatumPlane016]
  Width = 60
FEATURE [PartDesign::Pad] Pad005  label="Olimex Breakout Board PCB"
  Direction = (0,0,1)
  Length = 10
  Length2 = 10
  Profile = -> Sketch011
  ReferenceAxis = -> Sketch011 [N_Axis]
  Type = 3
  UpToFace = -> DatumPlane017
FEATURE [Sketcher::SketchObject] Sketch012
  ExternalGeometry = -> [Pad005]
  FullyConstrained = true
  MapMode = 5
  Placement = pos=(0,0,1.6) rot=(0,0,1;0rad)
  Support = -> [DatumPlane017]
  sketch-geometry (3):
    g0: Circle CenterX=-3.5 CenterY=7.5 CenterZ=0 NormalX=0 NormalY=0 NormalZ=1 AngleXU=0 Radius=1.5
    g1: Circle CenterX=19.5 CenterY=7.5 CenterZ=0 NormalX=0 NormalY=0 NormalZ=1 AngleXU=0 Radius=1.5
    g2: LineSegment StartX=-3.5 StartY=7.5 StartZ=0 EndX=19.5 EndY=7.5 EndZ=0
  constraints (8):
    c: Equal(g0,g1)
    c: Coincident(g2,g0)
    c: Coincident(g2,g1)
    c: Horizontal(g2)
    c: DistanceY(g1,g-5) = 17
    c: DistanceX(g1,g-5) = 4
    c: DistanceX(g2,g2) = 23
    c: Diameter(g0) = 3
FEATURE [PartDesign::Pocket] Pocket006  label="Olimex Breakout Board Mounting Holes"
  BaseFeature = -> Pad005
  Direction = (0,0,-1)
  Length = 0
  Length2 = 5
  Profile = -> Sketch012
  ReferenceAxis = -> Sketch012 [N_Axis]
  Type = 3
  UpToFace = -> DatumPlane016
FEATURE [PartDesign::Plane] DatumPlane018  label="Olimex Breakout Board RJ45 Top"
  AttachmentOffset = pos=(0,0,11.5) rot=(0,0,1;0rad)
  Length = 60
  MapMode = 5
  Placement = pos=(0,0,13.1) rot=(0,0,1;0rad)
  ResizeMode = 0
  Support = -> [DatumPlane017]
  Width = 60
FEATURE [PartDesign::Plane] DatumPlane019  label="Olimex Breakout Board Pin Header Top"
  AttachmentOffset = pos=(0,0,17) rot=(0,0,1;0rad)
  Length = 60
  MapMode = 5
  Placement = pos=(0,0,18.6) rot=(0,0,1;0rad)
  ResizeMode = 0
  Support = -> [DatumPlane017]
  Width = 60
FEATURE [Sketcher::SketchObject] Sketch015
  FullyConstrained = true
  MapMode = 5
  Placement = pos=(0,0,1.6) rot=(0,0,1;0rad)
  Support = -> [DatumPlane017]
  sketch-geometry (4):
    g0: LineSegment StartX=0.5 StartY=21 StartZ=0 EndX=15.5 EndY=21 EndZ=0
    g1: LineSegment StartX=15.5 StartY=21 StartZ=0 EndX=15.5 EndY=3 EndZ=0
    g2: LineSegment StartX=15.5 StartY=3 StartZ=0 EndX=0.5 EndY=3 EndZ=0
    g3: LineSegment StartX=0.5 StartY=3 StartZ=0 EndX=0.5 EndY=21 EndZ=0
  constraints (12):
    c: Coincident(g0,g1)
    c: Coincident(g1,g2)
    c: Coincident(g2,g3)
    c: Coincident(g3,g0)
    c: Horizontal(g0)
    c: Horizontal(g2)
    c: Vertical(g1)
    c: Vertical(g3)
    c: DistanceX(g0,g0) = 15
    c: DistanceY(g1,g1) = 18
    c: DistanceX(g-1,g2) = 0.5
    c: DistanceY(g-1,g2) = 3
FEATURE [PartDesign::Pad] Pad006  label="Olimex Breakout Board RJ45"
  BaseFeature = -> Pocket006
  Direction = (0,0,1)
  Length = 10
  Length2 = 10
  Profile = -> Sketch015
  ReferenceAxis = -> Sketch015 [N_Axis]
  Type = 3
  UpToFace = -> DatumPlane018 [Plane]
FEATURE [Sketcher::SketchObject] Sketch016
  FullyConstrained = true
  MapMode = 5
  Placement = pos=(0,0,1.6) rot=(0,0,1;0rad)
  Support = -> [DatumPlane017]
  sketch-geometry (4):
    g0: LineSegment StartX=-22 StartY=18 StartZ=0 EndX=-14 EndY=18 EndZ=0
    g1: LineSegment StartX=-14 StartY=18 StartZ=0 EndX=-14 EndY=-23 EndZ=0
    g2: LineSegment StartX=-14 StartY=-23 StartZ=0 EndX=-22 EndY=-23 EndZ=0
    g3: LineSegment StartX=-22 StartY=-23 StartZ=0 EndX=-22 EndY=18 EndZ=0
  constraints (12):
    c: Coincident(g0,g1)
    c: Coincident(g1,g2)
    c: Coincident(g2,g3)
    c: Coincident(g3,g0)
    c: Horizontal(g0)
    c: Horizontal(g2)
    c: Vertical(g1)
    c: Vertical(g3)
    c: DistanceX(g0,g0) = 8
    c: DistanceY(g3,g3) = 41
    c: DistanceY(g1,g-1) = 23
    c: DistanceX(g1,g-1) = 14
FEATURE [PartDesign::Pad] Pad007  label="Olimex Breakout Board Pin Header"
  BaseFeature = -> Pad006
  Direction = (0,0,1)
  Length = 10
  Length2 = 10
  Profile = -> Sketch016
  ReferenceAxis = -> Sketch016 [N_Axis]
  Type = 3
  UpToFace = -> DatumPlane019 [Plane]
FEATURE [PartDesign::Body] Body  label="Olimex Breakout Board Body"
  Group = -> [Sketch011,DatumPlane016,DatumPlane017,Pad005,Sketch012,Pocket006,DatumPlane018,Sketch015,Pad006,DatumPlane019,Sketch016,Pad007]
  Origin = -> Origin007
  Placement = pos=(-8,14.2,11) rot=(0,0,1;0rad)
  Tip = -> Pad007
PROVENANCE & LICENSES
A FreeCAD (.FCStd) document from a public repository crawl; recipes are the document's own serialized feature recipes (and, for linked parts, companion documents' recipes).
License: as declared in the source repository (recorded in the dataset sidecar).
